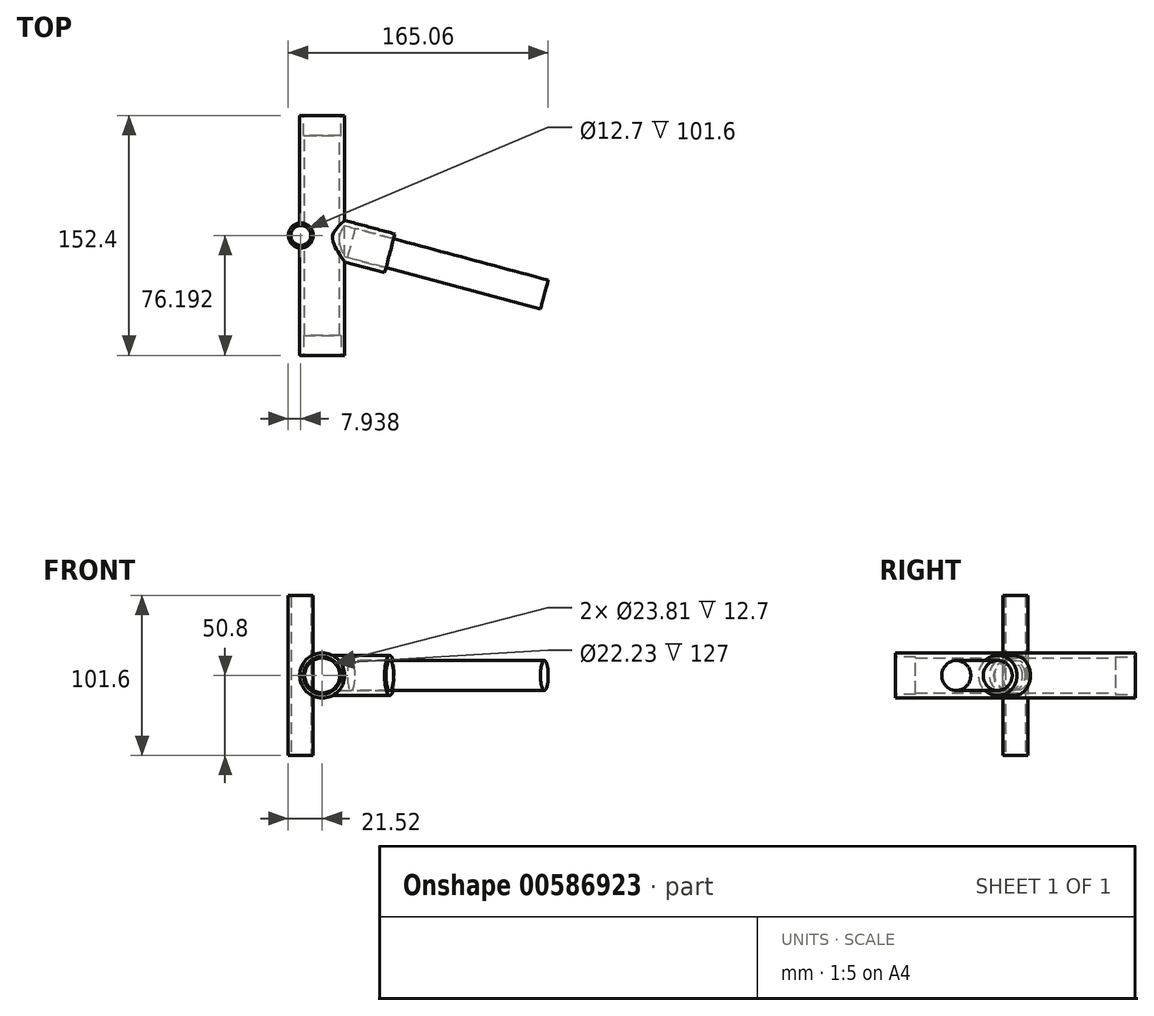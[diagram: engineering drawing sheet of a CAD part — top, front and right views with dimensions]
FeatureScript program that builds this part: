
annotation { "Feature Type Name" : "Feature", "Feature Type Description" : "" }
export const myFeature = defineFeature(function(context is Context, id is Id, definition is map)
    precondition{}
    {
        {
            var Q0;
            Q0=qCreatedBy(makeId("Front.planeOp"),FACE);
            var sketch = newSketch(context, id + "F0", { "sketchPlane" : qUnion([Q0])});
            skCircle(sketch, "E0", {"center": v(0, 0) * mm, "radius": 14.29 * mm});
            skCircle(sketch, "E1", {"center": v(0, 0) * mm, "radius": 11.11 * mm});
            skSolve(sketch);
        }
        {
            var Q0;
            Q0=makeQuery(id+"F0.imprint","IMPRINT",FACE,{"disambiguationData":[TD([[makeQuery(id+"F0.imprint","IMPRINT",EDGE,{"derivedFrom":sQuery(id+"F0.wireOp",EDGE,"E0")}),1.0]])]});
            extrude(context, id + "F1", {"entities" : qUnion([Q0]), "depth" : 152.4 * mm, "offsetDistance" : 25.4 * mm});
        }
        {
            var Q0;
            Q0=makeQuery(id+"F1.opExtrude","CAP_FACE",FACE,{"disambiguationData":[OSD([sQuery(id+"F0.wireOp",EDGE,"E0"),sQuery(id+"F0.wireOp",EDGE,"E1")])],"isStart":false});
            var sketch = newSketch(context, id + "F2", { "sketchPlane" : qUnion([Q0])});
            skCircle(sketch, "E2", {"center": v(0, 0) * mm, "radius": 11.9 * mm});
            skSolve(sketch);
        }
        {
            var Q0;
            Q0 = qSketchRegion(id + "F2", true);
            extrude(context, id + "F3", {"entities" : qUnion([Q0]), "operationType" : NewBodyOperationType.REMOVE, "oppositeDirection" : true, "depth" : 12.7 * mm, "offsetDistance" : 25.4 * mm});
        }
        {
            var Q0;
            Q0=makeQuery(id+"F1.opExtrude","CAP_FACE",FACE,{"disambiguationData":[OSD([sQuery(id+"F0.wireOp",EDGE,"E0"),sQuery(id+"F0.wireOp",EDGE,"E1")])],"isStart":true});
            var sketch = newSketch(context, id + "F4", { "sketchPlane" : qUnion([Q0])});
            skCircle(sketch, "E3", {"center": v(0, 0) * mm, "radius": 11.9 * mm});
            skSolve(sketch);
        }
        {
            var Q0;
            Q0 = qSketchRegion(id + "F4", true);
            extrude(context, id + "F5", {"entities" : qUnion([Q0]), "operationType" : NewBodyOperationType.REMOVE, "oppositeDirection" : true, "depth" : 12.7 * mm, "offsetDistance" : 25.4 * mm});
        }
        {
            var Q0;
            Q0=qCreatedBy(makeId("Top.planeOp"),FACE);
            var sketch = newSketch(context, id + "F6", { "sketchPlane" : qUnion([Q0])});
            skCircle(sketch, "E4", {"center": v(-13.58, -76.2) * mm, "radius": 7.94 * mm});
            skSolve(sketch);
        }
        {
            var Q0;
            Q0 = qSketchRegion(id + "F6", true);
            extrude(context, id + "F7", {"entities" : qUnion([Q0]), "operationType" : NewBodyOperationType.ADD, "depth" : 101.6 * mm, "offsetDistance" : 25.4 * mm, "symmetric" : true});
        }
        {
            var Q0;
            Q0=makeQuery(id+"F7.opExtrude","CAP_FACE",FACE,{"disambiguationData":[OSD([sQuery(id+"F6.wireOp",EDGE,"E4")])],"isStart":true});
            var sketch = newSketch(context, id + "F8", { "sketchPlane" : qUnion([Q0])});
            skCircle(sketch, "E5", {"center": v(-13.58, 76.2) * mm, "radius": 6.35 * mm});
            skSolve(sketch);
        }
        {
            var Q0;
            Q0 = qSketchRegion(id + "F8", true);
            extrude(context, id + "F9", {"entities" : qUnion([Q0]), "operationType" : NewBodyOperationType.REMOVE, "endBound" : BoundingType.THROUGH_ALL, "oppositeDirection" : true, "depth" : 25.4 * mm, "offsetDistance" : 25.4 * mm});
        }
        {
            var Q0;
            Q0=qCreatedBy(makeId("Right.planeOp"),FACE);
            var sketch = newSketch(context, id + "F10", { "sketchPlane" : qUnion([Q0])});
            skLineSegment(sketch, "E6", {"start": v(-76, -14.44) * mm, "end": v(-76, 14.69) * mm});
            skSolve(sketch);
        }
        {
            var Q0;
            Q0=sQuery(id+"F10.wireOp",EDGE,"E6");
            cPlane(context, id + "F11", {"entities" : qUnion([Q0]), "cplaneType" : CPlaneType.LINE_ANGLE, "offset" : 25.4 * mm, "angle" : 15 * degree, "oppositeDirection" : true, "width" : 152.4 * mm, "height" : 152.4 * mm});
        }
        {
            var Q0;
            Q0=qCreatedBy(id+"F11.planeOp",FACE);
            cPlane(context, id + "F12", {"entities" : qUnion([Q0]), "cplaneType" : CPlaneType.OFFSET, "offset" : 19.05 * mm, "width" : 152.4 * mm, "height" : 152.4 * mm});
        }
        {
            var Q0;
            Q0=qCreatedBy(id+"F12.planeOp",FACE);
            var sketch = newSketch(context, id + "F13", { "sketchPlane" : qUnion([Q0])});
            skCircle(sketch, "E7", {"center": v(-73.4, 0) * mm, "radius": 9.53 * mm});
            skCircle(sketch, "E8", {"center": v(-73.4, 0) * mm, "radius": 12.7 * mm});
            skSolve(sketch);
        }
        {
            var Q0;
            Q0=makeQuery(id+"F13.imprint","IMPRINT",FACE,{"disambiguationData":[TD([[makeQuery(id+"F13.imprint","IMPRINT",EDGE,{"derivedFrom":sQuery(id+"F13.wireOp",EDGE,"E7")}),-1.0]])]});
            extrude(context, id + "F14", {"entities" : qUnion([Q0]), "operationType" : NewBodyOperationType.ADD, "endBound" : BoundingType.UP_TO_NEXT, "oppositeDirection" : true, "depth" : 25.4 * mm, "offsetDistance" : 25.4 * mm});
        }
        {
            var Q0;
            Q0=makeQuery(id+"F14.opExtrude","CAP_FACE",FACE,{"disambiguationData":[OSD([sQuery(id+"F13.wireOp",EDGE,"E7"),sQuery(id+"F13.wireOp",EDGE,"E8")])],"isStart":true});
            extrude(context, id + "F15", {"entities" : qUnion([Q0]), "operationType" : NewBodyOperationType.ADD, "depth" : 25.4 * mm, "offsetDistance" : 25.4 * mm});
        }
        {
            var Q0;
            Q0=qCreatedBy(id+"F12.planeOp",FACE);
            var sketch = newSketch(context, id + "F16", { "sketchPlane" : qUnion([Q0])});
            skCircle(sketch, "E9.0", {"center": v(-73.4, 0) * mm, "radius": 9.52 * mm});
            skSolve(sketch);
        }
        {
            var Q0;
            Q0=makeQuery(id+"F16.imprint","IMPRINT",FACE,{"disambiguationData":[TD([[makeQuery(id+"F16.imprint","IMPRINT",EDGE,{"derivedFrom":sQuery(id+"F16.wireOp",EDGE,"E9.0")}),1.0]])]});
            extrude(context, id + "F17", {"entities" : qUnion([Q0]), "depth" : 127 * mm, "offsetDistance" : 25.4 * mm});
        }
    });
